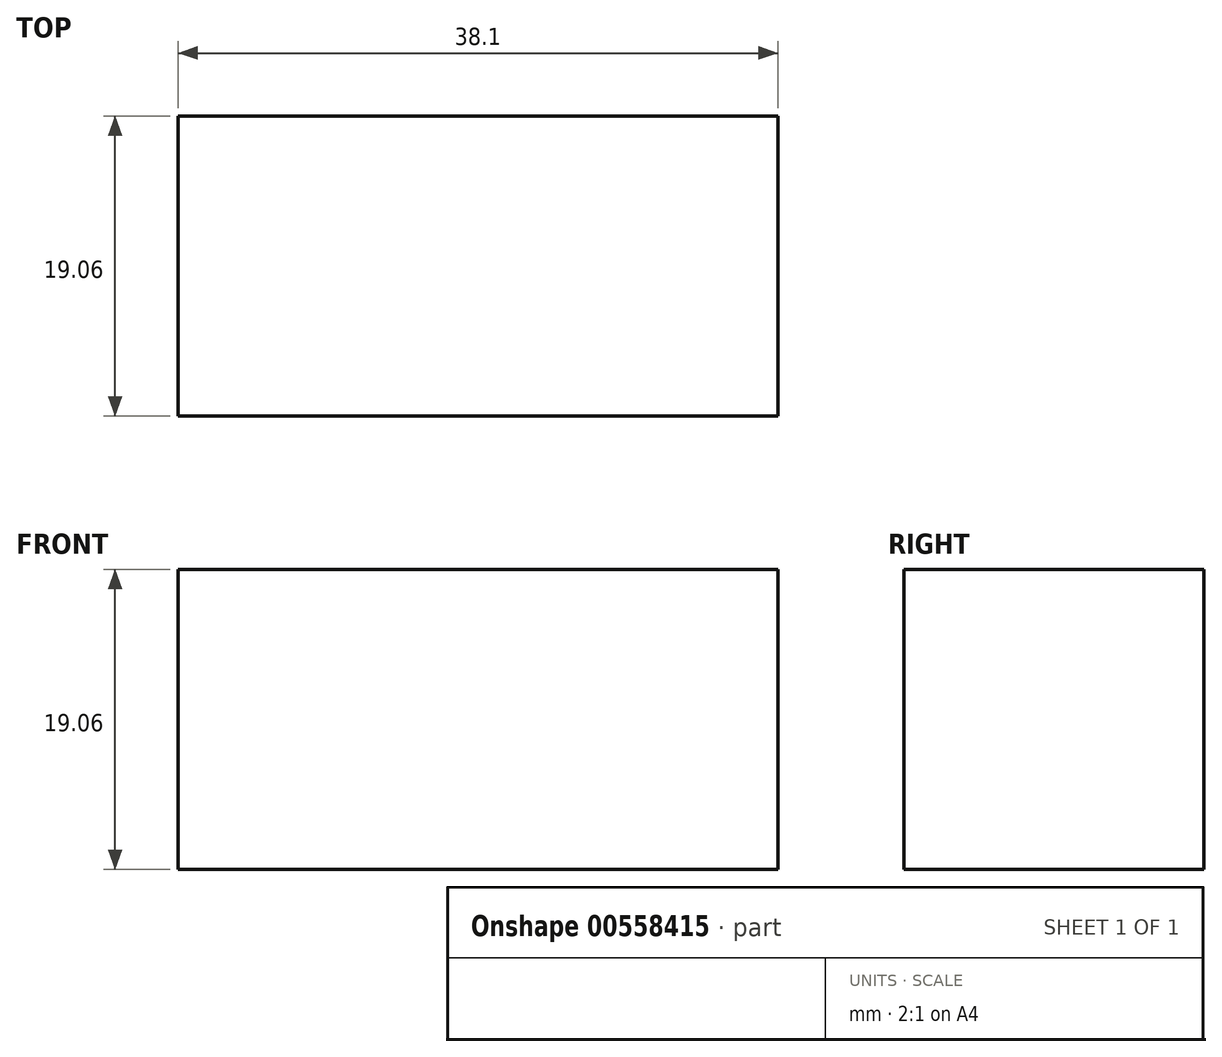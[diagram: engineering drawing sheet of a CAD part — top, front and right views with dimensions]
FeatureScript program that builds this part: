
annotation { "Feature Type Name" : "Feature", "Feature Type Description" : "" }
export const myFeature = defineFeature(function(context is Context, id is Id, definition is map)
    precondition{}
    {
        {
            var Q0;
            Q0=qCreatedBy(makeId("Front.planeOp"),FACE);
            var sketch = newSketch(context, id + "F0", { "sketchPlane" : qUnion([Q0])});
            skLineSegment(sketch, "E0.bottom", {"start": v(19.05, 9.53) * mm, "end": v(-19.05, 9.53) * mm});
            skLineSegment(sketch, "E0.top", {"start": v(19.05, -9.53) * mm, "end": v(-19.05, -9.53) * mm});
            skLineSegment(sketch, "E0.left", {"start": v(19.05, 9.53) * mm, "end": v(19.05, -9.53) * mm});
            skLineSegment(sketch, "E0.right", {"start": v(-19.05, 9.53) * mm, "end": v(-19.05, -9.53) * mm});
            skPoint(sketch, "E0.middle", {"position": v(0, 0) * mm});
            skSolve(sketch);
        }
        {
            var Q0;
            Q0=makeQuery(id+"F0.imprint","IMPRINT",FACE,{"disambiguationData":[TD([[makeQuery(id+"F0.imprint","IMPRINT",EDGE,{"derivedFrom":sQuery(id+"F0.wireOp",EDGE,"E0.bottom")}),1.0]])]});
            extrude(context, id + "F1", {"entities" : qUnion([Q0]), "endBound" : BoundingType.SYMMETRIC, "depth" : 19.05 * mm, "offsetDistance" : 25.4 * mm});
        }
    });
